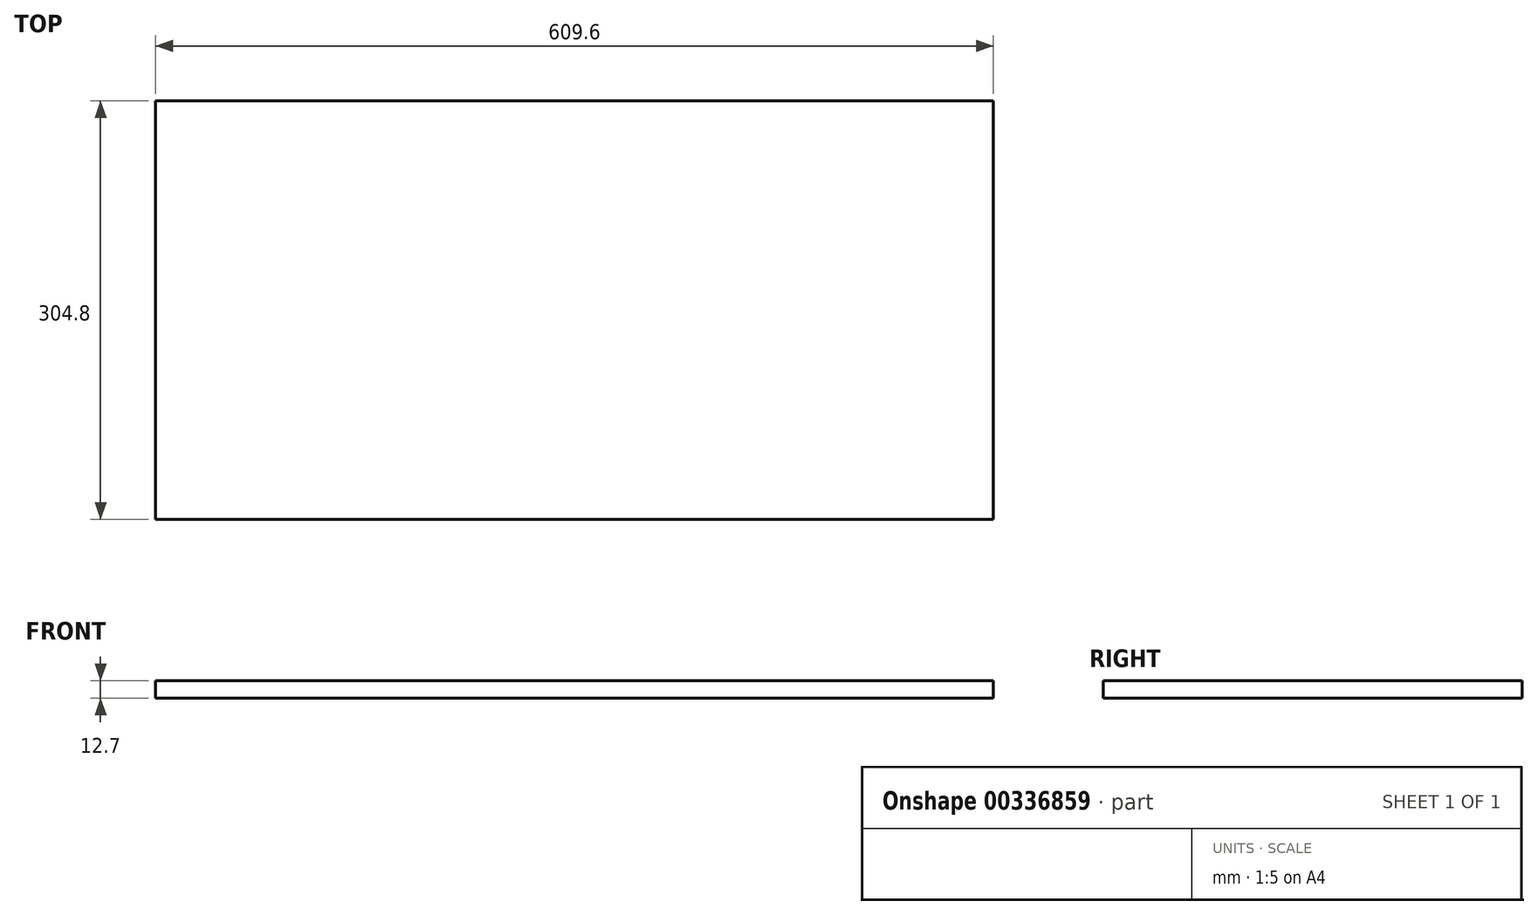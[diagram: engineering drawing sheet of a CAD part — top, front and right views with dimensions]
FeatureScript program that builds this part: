
annotation { "Feature Type Name" : "Feature", "Feature Type Description" : "" }
export const myFeature = defineFeature(function(context is Context, id is Id, definition is map)
    precondition{}
    {
        {
            var Q0;
            Q0=qCreatedBy(makeId("Top.planeOp"),FACE);
            var sketch = newSketch(context, id + "F0", { "sketchPlane" : qUnion([Q0])});
            skLineSegment(sketch, "E0.bottom", {"start": v(-150.48, 447.34) * mm, "end": v(154.32, 447.34) * mm});
            skLineSegment(sketch, "E0.top", {"start": v(-150.48, -162.26) * mm, "end": v(154.32, -162.26) * mm});
            skLineSegment(sketch, "E0.left", {"start": v(-150.48, 447.34) * mm, "end": v(-150.48, -162.26) * mm});
            skLineSegment(sketch, "E0.right", {"start": v(154.32, 447.34) * mm, "end": v(154.32, -162.26) * mm});
            skSolve(sketch);
        }
        {
            var Q0;
            Q0=makeQuery(id+"F0.imprint","IMPRINT",FACE,{"disambiguationData":[TD([[makeQuery(id+"F0.imprint","IMPRINT",EDGE,{"derivedFrom":sQuery(id+"F0.wireOp",EDGE,"E0.bottom")}),-1.0]])]});
            extrude(context, id + "F1", {"entities" : qUnion([Q0]), "depth" : 12.7 * mm});
        }
        {
            var Q0;
            Q0=makeQuery(id+"F1.opExtrude","SWEPT_BODY",BODY,{"disambiguationData":[OSD([sQuery(id+"F0.wireOp",EDGE,"E0.bottom"),sQuery(id+"F0.wireOp",EDGE,"E0.top"),sQuery(id+"F0.wireOp",EDGE,"E0.left"),sQuery(id+"F0.wireOp",EDGE,"E0.right")])]});
            var Q1;
            Q1=makeQuery(id+"F1.opExtrude","SWEPT_EDGE",EDGE,{"disambiguationData":[OSD([sQuery(id+"F0.wireOp",EDGE,"E0.top"),sQuery(id+"F0.wireOp",EDGE,"E0.right")])]});
            transform(context, id + "F2", {"entities" : qUnion([Q0]), "transformType" : TransformType.ROTATION, "transformAxis" : qUnion([Q1]), "angle" : 90 * degree, "makeCopy" : false});
        }
    });
